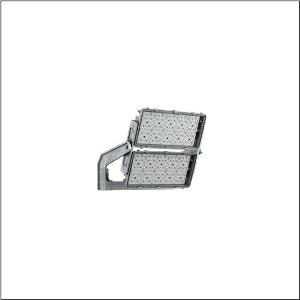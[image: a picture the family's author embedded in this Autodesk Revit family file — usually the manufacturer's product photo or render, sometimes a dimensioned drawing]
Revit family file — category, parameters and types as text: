
# Revit family: floodlight_fl_11_maxi_remote___rs07_5xa779514k01ba_6340
name_source: partatom
category: Lighting Fixtures
units: mm (PartAtom-declared; Revit-internal decimal feet)

## family parameters
Cut with Voids When Loaded = No
Host = Face
Light Source = No
Part Type = Normal
Room Calculation Point = No
Round Connector Dimension = Use Diameter
Shared = No

## types (1)
- --- (1 x LED, 75300 lm, 707.9 W, 5700K)
    Apparent Load = 708 VA
    CIE Flux Codes = 80 93 99 100 99
    Color Rendering = 90
    Color Temperature = 5700K
    Default Elevation = 1800 mm
    Description = Floodlight FL 11  maxi  Remote floodlight; light control with lens of PMMA; cover panel of toughened safety glass, transparent; light distribution: RS07, rotationally symmetric direct distribution, LEDcolour temperature: 5700K, rated luminous flux: 75.300lm, colour rendering: CRI > 90, light colour: 957; luminous efficacy: 106lm/W; brightness control: DMX+RDM; with terminal, 8-pole, max. 2.5mm², mains connection: 220..240V/380..400V AC, 50/60Hz, surge voltage resistance: line to ground: 10kV, ECG replaceable separately, LED unit replaceable without ESD environment, dustproof LED module, dimming range 10..100%; 708W floodlight with 2x LED unit of diecast aluminium, coated grey; length: 713mm / width: 651mm / height: 338mm; mounting bracket, of diecast aluminium, uncoated, natural, equipment: Longlife, protection rating (complete): IP66; insulation class (complete): insulation class I (protective earthing); certification: CE, ENEC, VDE; ball protection: ball impact resistance with accessories, impact resistance: IK07; only for outdoor installations, rated ambient temperature 10°C, permissible operating ambient temperature: -40..+40°C, permissible storage temperature: -40..+85°C; packaging unit: 1 piece

Light Distribution: RS07
    Height = 320 mm
    Lamp = 1 x LED
    Lamp Light Flux = 75300 lm
    Lamp Power = 707.9 W
    Lamp count = 1
    Length = 712 mm
    Luminous efficacy = 106 lm/W
    Manufacturer = Siteco
    ModVariant = No
    Model = 5XA779514K01BA
    Mounting Place = Ceiling
    Mounting Type = Surface mounted
    Number of Poles = 1
    OnlyDefault = Yes
    Power Factor = 1
    Product Name = Floodlight FL 11 maxi Remote | RS07
    Product group = floodlight | ceiling mounted
    ProductGroupID = 303
    Protection Class = Protection class I
    Protection Degree = IP 66
    RLX_Detail_Level = 1
    RLX_Emergency_Light_Flux = 0 lm
    RLX_Emergency_Type = 0
    RLX_Emergency_Type_DB = No
    RlxData = <blob elided: 41229 chars, md5=cb5a7bf2>
    Socket = socket
    Standby Power = 0 W
    System Light Flux = 75300 lm
    System Power = 708 W
    Type Comments = factory setting: luminous flux: 100 % | dim-lin: 254 | 740 mA
    Type Image = l_1006788.jpg
    URL = http://relux.com
    VarID = @adj_132855
    Voltage = 0 V
    Weight = 0.00 kg
    Width = 655 mm

## geometry (parser evidence)
native form markers: Blend x4, Sweep x12
no freeform markers — native parametric forms only
